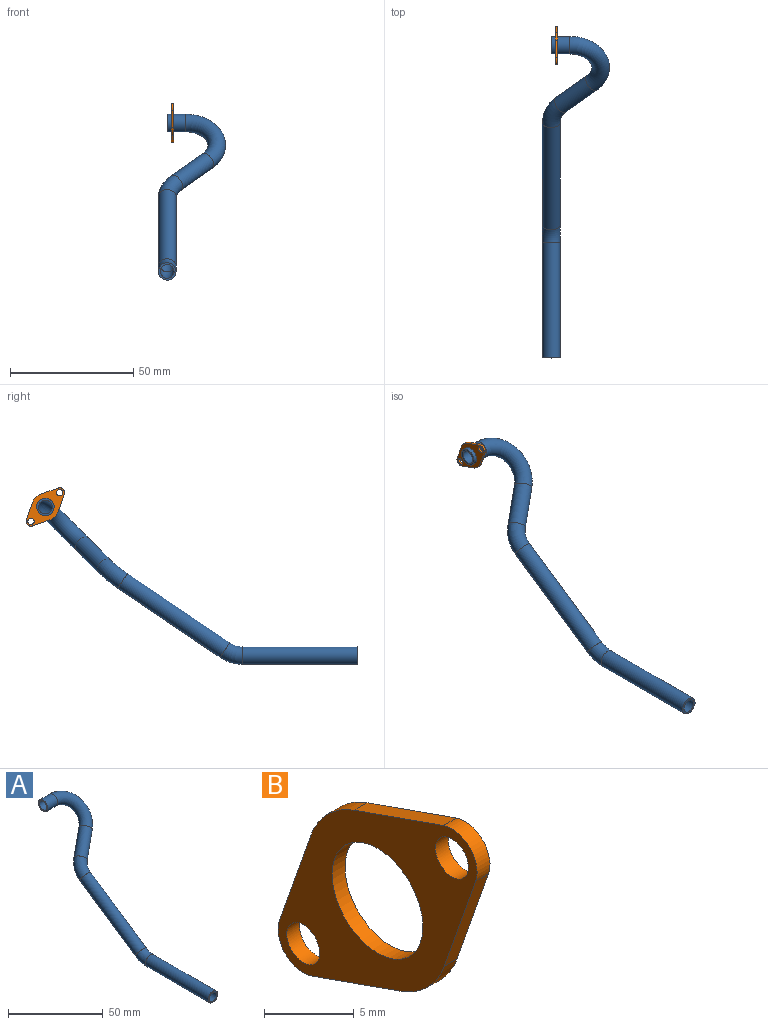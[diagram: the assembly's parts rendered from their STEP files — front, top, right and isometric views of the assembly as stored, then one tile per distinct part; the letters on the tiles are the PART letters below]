
ASSEMBLY  parts=2 mates=1
PART A: 16 faces, bbox 29.9x130.6x68.8 mm
  f0: cylinder r=2.78mm len=46.9mm, axis (0,1,0), area 819.6mm2, adj f1,f7
  f1: torus R=12.7mm, axis (1,0,0), area 132.2mm2, adj f0,f2
  f2: cylinder r=2.78mm len=44.69mm, axis (0,0.83,0.56), area 877.5mm2, adj f1,f3
  f3: torus R=12.7mm, axis (0.19,0.55,-0.81), area 178.3mm2, adj f2,f4
  f4: cylinder r=2.78mm len=16.54mm, axis (0.71,0.5,0.5), area 311.5mm2, adj f3,f5
  f5: torus R=12.7mm, axis (0,-0.71,0.71), area 522.9mm2, adj f4,f6
  f6: cylinder r=2.78mm len=7.44mm, axis (-1,0,0), area 130mm2, adj f5,f8
  f7: plane 7.14x7.14mm, normal (0,-1,0), area 15.7mm2, adj f0,f9
  f8: plane 7.14x7.14mm, normal (-1,0,0), area 15.7mm2, adj f6,f15
  f9: cylinder r=3.57mm len=46.9mm, axis (0,1,0), area 1051.7mm2, adj f7,f10
  f10: torus R=12.7mm, axis (1,0,0), area 169.6mm2, adj f9,f11
  f11: cylinder r=3.57mm len=45.57mm, axis (0,0.83,0.56), area 1126mm2, adj f10,f12
  f12: torus R=12.7mm, axis (0.19,0.55,-0.81), area 228.7mm2, adj f11,f13
  f13: cylinder r=3.57mm len=17.65mm, axis (0.71,0.5,0.5), area 399.7mm2, adj f12,f14
  f14: torus R=12.7mm, axis (0,-0.71,0.71), area 671mm2, adj f13,f15
  f15: cylinder r=3.57mm len=7.44mm, axis (-1,0,0), area 166.8mm2, adj f8,f14
PART B: 13 faces, bbox 1x15.6x15.6 mm
  f0: plane 7.03x2.48mm, normal (0,-0.94,-0.33), area 7.6mm2, adj f1,f8,f9,f10
  f1: cylinder r=5.55mm len=3.39mm, axis (-1,0,0), area 5mm2, adj f0,f2,f9,f10
  f2: plane 7.03x2.48mm, normal (0,-0.33,-0.94), area 7.6mm2, adj f1,f3,f9,f10
  f3: cylinder r=1.98mm len=2.64mm, axis (-1,0,0), area 4.5mm2, adj f2,f4,f9,f10
  f4: plane 7.03x2.48mm, normal (0,0.94,0.33), area 7.6mm2, adj f3,f5,f9,f10
  f5: cylinder r=5.55mm len=3.39mm, axis (-1,0,0), area 5mm2, adj f4,f6,f9,f10
  f6: plane 7.03x2.48mm, normal (0,0.33,0.94), area 7.6mm2, adj f5,f8,f9,f10
  f7: cylinder r=3.57mm len=7.14mm, axis (-1,0,0), area 22.8mm2, adj f9,f10
  f8: cylinder r=1.98mm len=2.64mm, axis (-1,0,0), area 4.5mm2, adj f0,f6,f9,f10
  f9: plane 15.65x15.65mm, normal (1,0,0), area 98mm2, adj f0,f1,f2,f3,f4,f5,f6,f7
  f10: plane 15.65x15.65mm, normal (-1,0,0), area 98mm2, adj f0,f1,f2,f3,f4,f5,f6,f7
  f11: cylinder r=1.3mm len=2.59mm, axis (-1,0,0), area 8.3mm2, adj f9,f10
  f12: cylinder r=1.3mm len=2.59mm, axis (-1,0,0), area 8.3mm2, adj f9,f10
PLACE A at identity fixed
PLACE B t=(1.57,0,0)mm
MATE fastened B.f7 <-> A.f6  axis (-1,0,0) through (1.57,0,0)mm
